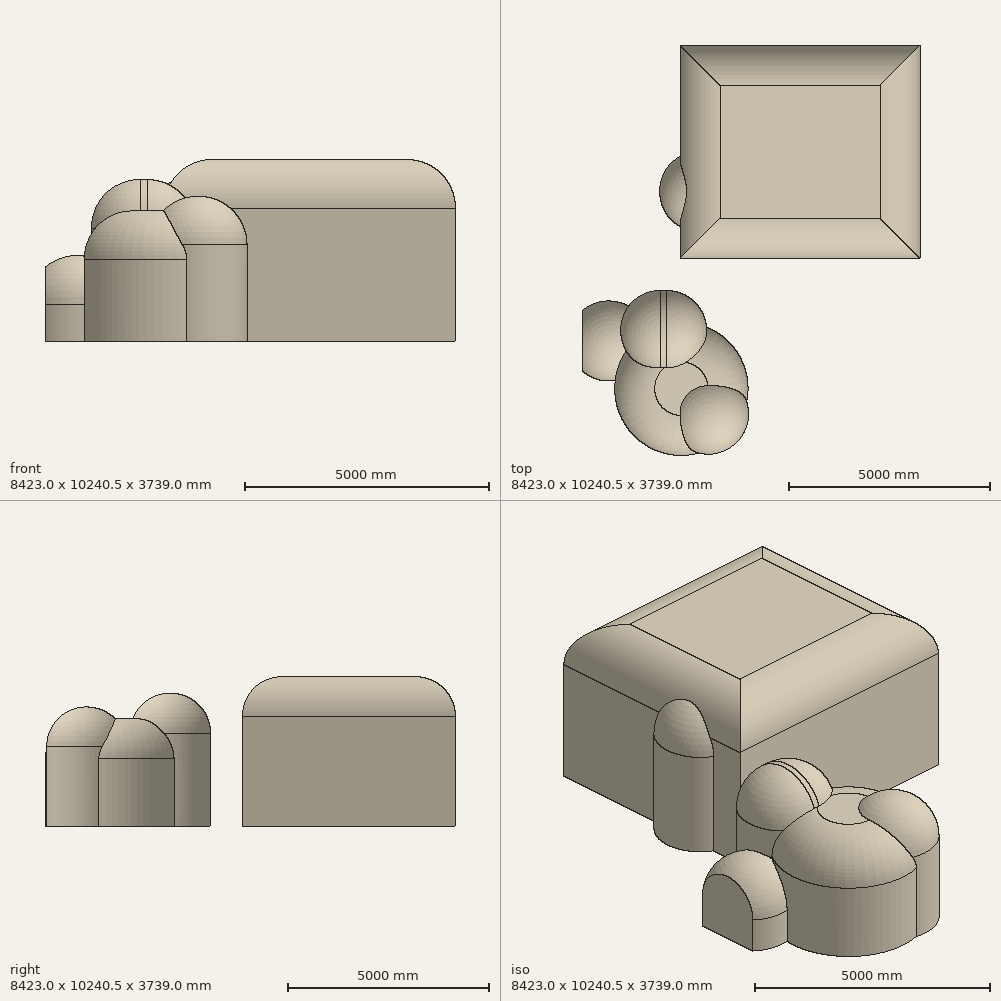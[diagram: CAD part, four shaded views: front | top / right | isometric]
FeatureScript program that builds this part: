
annotation { "Feature Type Name" : "Feature", "Feature Type Description" : "" }
export const myFeature = defineFeature(function(context is Context, id is Id, definition is map)
    precondition{}
    {
        {
            var Q0;
            Q0=qCreatedBy(makeId("Top.planeOp"),FACE);
            var sketch = newSketch(context, id + "F0", { "sketchPlane" : qUnion([Q0])});
            skLineSegment(sketch, "E0", {"start": v(0, 0) * mm, "end": v(7972, 0) * mm});
            skLineSegment(sketch, "E1", {"start": v(0, 0) * mm, "end": v(0, 5130) * mm});
            skLineSegment(sketch, "E2", {"start": v(0, 5130) * mm, "end": v(355, 5130) * mm});
            skLineSegment(sketch, "E3", {"start": v(355, 5130) * mm, "end": v(355, 15952) * mm});
            skLineSegment(sketch, "E4.bottom", {"start": v(2435, 10830) * mm, "end": v(8423, 10830) * mm});
            skLineSegment(sketch, "E4.top", {"start": v(2435, 5511) * mm, "end": v(8423, 5511) * mm});
            skLineSegment(sketch, "E4.left", {"start": v(2435, 10830) * mm, "end": v(2435, 5511) * mm});
            skLineSegment(sketch, "E4.right", {"start": v(8423, 10830) * mm, "end": v(8423, 5511) * mm});
            skCircle(sketch, "E5", {"center": v(2917, 7181) * mm, "radius": 1000 * mm});
            skCircle(sketch, "E6", {"center": v(650, 3450) * mm, "radius": 1000 * mm});
            skArc(sketch, "E7", {"start": v(1944, 4712) * mm, "mid": v(944, 3712) * mm, "end": v(1944, 2712) * mm});
            skArc(sketch, "E8", {"start": v(2091, 2712) * mm, "mid": v(3091, 3712) * mm, "end": v(2091, 4712) * mm});
            skLineSegment(sketch, "E9", {"start": v(1944, 4712) * mm, "end": v(2091, 4712) * mm});
            skLineSegment(sketch, "E10", {"start": v(1944, 2712) * mm, "end": v(2091, 2712) * mm});
            skCircle(sketch, "E11", {"center": v(3141, 1620) * mm, "radius": 1000 * mm});
            skSolve(sketch);
        }
        {
            var Q0;
            {var subQ0=sQuery(id+"F0.wireOp",EDGE,"E5");var subQ1=sQuery(id+"F0.wireOp",EDGE,"E4.left");var subQ2=makeQuery(id+"F0.imprint","INTERSECT",VERTEX,{"disambiguationData":[OD(0.0)],"derivedFrom":[subQ1,subQ0]});Q0=makeQuery(id+"F0.imprint","IMPRINT",FACE,{"disambiguationData":[TD([[makeQuery(id+"F0.imprint","IMPRINT",EDGE,{"disambiguationData":[TD([[subQ2,-1.0]])],"derivedFrom":subQ1}),-1.0]])]});}
            var Q1;
            {var subQ0=sQuery(id+"F0.wireOp",EDGE,"E5");var subQ1=sQuery(id+"F0.wireOp",EDGE,"E4.left");var subQ2=makeQuery(id+"F0.imprint","INTERSECT",VERTEX,{"disambiguationData":[OD(0.0)],"derivedFrom":[subQ1,subQ0]});Q1=makeQuery(id+"F0.imprint","IMPRINT",FACE,{"disambiguationData":[TD([[makeQuery(id+"F0.imprint","IMPRINT",EDGE,{"disambiguationData":[TD([[subQ2,-1.0]])],"derivedFrom":subQ1}),1.0]])]});}
            extrude(context, id + "F1", {"entities" : qUnion([Q0, Q1]), "depth" : 3327 * mm});
        }
        {
            var Q0;
            Q0=makeQuery(id+"F1.opExtrude","CAP_EDGE",EDGE,{"disambiguationData":[OSD([sQuery(id+"F0.wireOp",EDGE,"E5")])],"isStart":false});
            fillet(context, id + "F2", {"entities" : qUnion([Q0]), "radius" : 1000 * mm, "tangentPropagation" : true, "allowEdgeOverflow" : false});
        }
        {
            var Q0;
            {var subQ4=sQuery(id+"F0.wireOp",EDGE,"E4.bottom");Q0=makeQuery(id+"F0.imprint","IMPRINT",FACE,{"disambiguationData":[TD([[makeQuery(id+"F0.imprint","IMPRINT",EDGE,{"derivedFrom":subQ4}),-1.0]])]});}
            var Q1;
            {var subQ0=sQuery(id+"F0.wireOp",EDGE,"E5");var subQ1=sQuery(id+"F0.wireOp",EDGE,"E4.left");var subQ2=makeQuery(id+"F0.imprint","INTERSECT",VERTEX,{"disambiguationData":[OD(0.0)],"derivedFrom":[subQ1,subQ0]});Q1=makeQuery(id+"F0.imprint","IMPRINT",FACE,{"disambiguationData":[TD([[makeQuery(id+"F0.imprint","IMPRINT",EDGE,{"disambiguationData":[TD([[subQ2,-1.0]])],"derivedFrom":subQ1}),1.0]])]});}
            extrude(context, id + "F3", {"entities" : qUnion([Q0, Q1]), "operationType" : NewBodyOperationType.ADD, "depth" : 3739 * mm});
        }
        {
            var Q0;
            Q0=makeQuery(id+"F3.opExtrude","CAP_EDGE",EDGE,{"disambiguationData":[OSD([sQuery(id+"F0.wireOp",EDGE,"E4.top")])],"isStart":false});
            var Q1;
            Q1=makeQuery(id+"F3.opExtrude","CAP_EDGE",EDGE,{"disambiguationData":[OSD([sQuery(id+"F0.wireOp",EDGE,"E4.right")])],"isStart":false});
            var Q2;
            Q2=makeQuery(id+"F3.opExtrude","CAP_EDGE",EDGE,{"disambiguationData":[OSD([sQuery(id+"F0.wireOp",EDGE,"E4.left")])],"isStart":false});
            var Q3;
            Q3=makeQuery(id+"F3.opExtrude","CAP_EDGE",EDGE,{"disambiguationData":[OSD([sQuery(id+"F0.wireOp",EDGE,"E4.bottom")])],"isStart":false});
            fillet(context, id + "F4", {"entities" : qUnion([Q0, Q1, Q2, Q3]), "radius" : 1000 * mm, "tangentPropagation" : true, "allowEdgeOverflow" : false});
        }
        {
            var Q0;
            {var subQ0=sQuery(id+"F0.wireOp",EDGE,"E6");var subQ1=sQuery(id+"F0.wireOp",EDGE,"E1");var subQ2=makeQuery(id+"F0.imprint","INTERSECT",VERTEX,{"disambiguationData":[OD(0.0)],"derivedFrom":[subQ1,subQ0]});Q0=makeQuery(id+"F0.imprint","IMPRINT",FACE,{"disambiguationData":[TD([[makeQuery(id+"F0.imprint","IMPRINT",EDGE,{"disambiguationData":[TD([[subQ2,1.0]])],"derivedFrom":subQ1}),-1.0]])]});}
            var Q1;
            {var subQ0=sQuery(id+"F0.wireOp",EDGE,"E7");var subQ1=sQuery(id+"F0.wireOp",EDGE,"E6");var subQ2=makeQuery(id+"F0.imprint","INTERSECT",VERTEX,{"disambiguationData":[OD(0.0)],"derivedFrom":[subQ1,subQ0]});Q1=makeQuery(id+"F0.imprint","IMPRINT",FACE,{"disambiguationData":[TD([[makeQuery(id+"F0.imprint","IMPRINT",EDGE,{"disambiguationData":[TD([[subQ2,1.0]])],"derivedFrom":subQ1}),1.0]])]});}
            extrude(context, id + "F5", {"entities" : qUnion([Q0, Q1]), "depth" : 1765 * mm});
        }
        {
            var Q0;
            Q0=makeQuery(id+"F5.opExtrude","CAP_EDGE",EDGE,{"disambiguationData":[OSD([sQuery(id+"F0.wireOp",EDGE,"E6")])],"isStart":false});
            fillet(context, id + "F6", {"entities" : qUnion([Q0]), "radius" : 1000 * mm, "tangentPropagation" : true, "allowEdgeOverflow" : false});
        }
        {
            var Q0;
            Q0=makeQuery(id+"F0.imprint","IMPRINT",FACE,{"disambiguationData":[TD([[makeQuery(id+"F0.imprint","IMPRINT",EDGE,{"derivedFrom":sQuery(id+"F0.wireOp",EDGE,"E8")}),1.0]])]});
            var Q1;
            {var subQ0=sQuery(id+"F0.wireOp",EDGE,"E7");var subQ1=sQuery(id+"F0.wireOp",EDGE,"E6");var subQ2=makeQuery(id+"F0.imprint","INTERSECT",VERTEX,{"disambiguationData":[OD(0.0)],"derivedFrom":[subQ1,subQ0]});Q1=makeQuery(id+"F0.imprint","IMPRINT",FACE,{"disambiguationData":[TD([[makeQuery(id+"F0.imprint","IMPRINT",EDGE,{"disambiguationData":[TD([[subQ2,1.0]])],"derivedFrom":subQ1}),1.0]])]});}
            extrude(context, id + "F7", {"entities" : qUnion([Q0, Q1]), "operationType" : NewBodyOperationType.ADD, "depth" : 3327 * mm});
        }
        {
            var Q0;
            Q0=makeQuery(id+"F7.opExtrude","CAP_EDGE",EDGE,{"disambiguationData":[OSD([sQuery(id+"F0.wireOp",EDGE,"E7")])],"isStart":false});
            fillet(context, id + "F8", {"entities" : qUnion([Q0]), "radius" : 1000 * mm, "tangentPropagation" : true, "allowEdgeOverflow" : false});
        }
        {
            var Q0;
            Q0=makeQuery(id+"F0.imprint","IMPRINT",FACE,{"disambiguationData":[TD([[makeQuery(id+"F0.imprint","IMPRINT",EDGE,{"derivedFrom":sQuery(id+"F0.wireOp",EDGE,"E11")}),1.0]])]});
            extrude(context, id + "F9", {"entities" : qUnion([Q0]), "depth" : 2984 * mm});
        }
        {
            var Q0;
            Q0=makeQuery(id+"F9.opExtrude","CAP_EDGE",EDGE,{"disambiguationData":[OSD([sQuery(id+"F0.wireOp",EDGE,"E11")])],"isStart":false});
            fillet(context, id + "F10", {"entities" : qUnion([Q0]), "radius" : 1000 * mm, "tangentPropagation" : true, "allowEdgeOverflow" : false});
        }
        {
            var Q0;
            Q0=qCreatedBy(makeId("Top.planeOp"),FACE);
            var sketch = newSketch(context, id + "F11", { "sketchPlane" : qUnion([Q0])});
            skCircle(sketch, "E12.0", {"center": v(650, 3450) * mm, "radius": 1000 * mm});
            skLineSegment(sketch, "E13.0", {"start": v(0, 0) * mm, "end": v(7972, 0) * mm});
            skLineSegment(sketch, "E14.0", {"start": v(0, 0) * mm, "end": v(0, 5130) * mm});
            skLineSegment(sketch, "E15.0", {"start": v(355, 5130) * mm, "end": v(355, 15952) * mm, "construction": true});
            skCircle(sketch, "E16", {"center": v(2461, 2256) * mm, "radius": 1666.5 * mm});
            skCircle(sketch, "E17", {"center": v(5761, 6751) * mm, "radius": 1000 * mm});
            skArc(sketch, "E18", {"start": v(4969.67, 9882.39) * mm, "mid": v(5149.61, 8479.67) * mm, "end": v(6552.33, 8659.61) * mm});
            skArc(sketch, "E19", {"start": v(6834.33, 9024.61) * mm, "mid": v(6654.39, 10427.33) * mm, "end": v(5251.67, 10247.39) * mm});
            skLineSegment(sketch, "E20", {"start": v(6552.33, 8659.61) * mm, "end": v(6834.33, 9024.61) * mm});
            skLineSegment(sketch, "E21", {"start": v(4969.67, 9882.39) * mm, "end": v(5251.67, 10247.39) * mm});
            skSolve(sketch);
        }
        {
            var Q0;
            {var subQ0=sQuery(id+"F11.wireOp",EDGE,"E14.0");var subQ1=sQuery(id+"F11.wireOp",EDGE,"E12.0");var subQ2=makeQuery(id+"F11.imprint","INTERSECT",VERTEX,{"disambiguationData":[OD(0.0)],"derivedFrom":[subQ1,subQ0]});Q0=makeQuery(id+"F11.imprint","IMPRINT",FACE,{"disambiguationData":[TD([[makeQuery(id+"F11.imprint","IMPRINT",EDGE,{"disambiguationData":[TD([[subQ2,1.0]])],"derivedFrom":subQ1}),1.0]])]});}
            var Q1;
            {var subQ0=sQuery(id+"F11.wireOp",EDGE,"E16");var subQ1=sQuery(id+"F11.wireOp",EDGE,"E12.0");var subQ2=makeQuery(id+"F11.imprint","INTERSECT",VERTEX,{"disambiguationData":[OD(0.0)],"derivedFrom":[subQ1,subQ0]});Q1=makeQuery(id+"F11.imprint","IMPRINT",FACE,{"disambiguationData":[TD([[makeQuery(id+"F11.imprint","IMPRINT",EDGE,{"disambiguationData":[TD([[subQ2,1.0]])],"derivedFrom":subQ1}),1.0]])]});}
            extrude(context, id + "F12", {"entities" : qUnion([Q0, Q1]), "depth" : 1400 * mm});
        }
        {
            var Q0;
            Q0=makeQuery(id+"F12.opExtrude","CAP_EDGE",EDGE,{"disambiguationData":[OSD([sQuery(id+"F11.wireOp",EDGE,"E12.0")])],"isStart":false});
            fillet(context, id + "F13", {"entities" : qUnion([Q0]), "radius" : 1000 * mm, "tangentPropagation" : true, "allowEdgeOverflow" : false});
        }
        {
            var Q0;
            {var subQ0=sQuery(id+"F11.wireOp",EDGE,"E16");var subQ1=sQuery(id+"F11.wireOp",EDGE,"E12.0");var subQ2=makeQuery(id+"F11.imprint","INTERSECT",VERTEX,{"disambiguationData":[OD(0.0)],"derivedFrom":[subQ1,subQ0]});Q0=makeQuery(id+"F11.imprint","IMPRINT",FACE,{"disambiguationData":[TD([[makeQuery(id+"F11.imprint","IMPRINT",EDGE,{"disambiguationData":[TD([[subQ2,1.0]])],"derivedFrom":subQ1}),-1.0]])]});}
            var Q1;
            {var subQ0=sQuery(id+"F11.wireOp",EDGE,"E16");var subQ1=sQuery(id+"F11.wireOp",EDGE,"E12.0");var subQ2=makeQuery(id+"F11.imprint","INTERSECT",VERTEX,{"disambiguationData":[OD(0.0)],"derivedFrom":[subQ1,subQ0]});Q1=makeQuery(id+"F11.imprint","IMPRINT",FACE,{"disambiguationData":[TD([[makeQuery(id+"F11.imprint","IMPRINT",EDGE,{"disambiguationData":[TD([[subQ2,1.0]])],"derivedFrom":subQ1}),1.0]])]});}
            extrude(context, id + "F14", {"entities" : qUnion([Q0, Q1]), "operationType" : NewBodyOperationType.ADD, "depth" : 2683 * mm});
        }
        {
            var Q0;
            Q0=makeQuery(id+"F14.opExtrude","CAP_EDGE",EDGE,{"disambiguationData":[OSD([sQuery(id+"F11.wireOp",EDGE,"E16")])],"isStart":false});
            fillet(context, id + "F15", {"entities" : qUnion([Q0]), "radius" : 1000 * mm, "tangentPropagation" : true, "allowEdgeOverflow" : false});
        }
        {
            var Q0;
            {var subQ0=sQuery(id+"F11.wireOp",EDGE,"E19");var subQ1=sQuery(id+"F11.wireOp",EDGE,"E18");var subQ2=makeQuery(id+"F11.imprint","INTERSECT",VERTEX,{"disambiguationData":[OD(0.0)],"derivedFrom":[subQ1,subQ0]});Q0=makeQuery(id+"F11.imprint","IMPRINT",FACE,{"disambiguationData":[TD([[makeQuery(id+"F11.imprint","IMPRINT",EDGE,{"disambiguationData":[TD([[subQ2,1.0]])],"derivedFrom":subQ1}),-1.0]])]});}
            var Q1;
            {var subQ0=sQuery(id+"F11.wireOp",EDGE,"E19");var subQ1=sQuery(id+"F11.wireOp",EDGE,"E18");var subQ2=makeQuery(id+"F11.imprint","INTERSECT",VERTEX,{"disambiguationData":[OD(0.0)],"derivedFrom":[subQ1,subQ0]});Q1=makeQuery(id+"F11.imprint","IMPRINT",FACE,{"disambiguationData":[TD([[makeQuery(id+"F11.imprint","IMPRINT",EDGE,{"disambiguationData":[TD([[subQ2,1.0]])],"derivedFrom":subQ1}),1.0]])]});}
            var Q2;
            Q2=makeQuery(id+"F11.imprint","IMPRINT",FACE,{"disambiguationData":[TD([[makeQuery(id+"F11.imprint","IMPRINT",EDGE,{"derivedFrom":sQuery(id+"F11.wireOp",EDGE,"E17")}),1.0]])]});
            extrude(context, id + "F16", {"entities" : qUnion([Q0, Q1, Q2]), "depth" : 2550 * mm});
        }
        {
            var Q0;
            Q0=makeQuery(id+"F16.opExtrude","CAP_EDGE",EDGE,{"disambiguationData":[OSD([sQuery(id+"F11.wireOp",EDGE,"E19")])],"isStart":false});
            var Q1;
            Q1=makeQuery(id+"F16.opExtrude","CAP_EDGE",EDGE,{"disambiguationData":[OSD([sQuery(id+"F11.wireOp",EDGE,"E17")])],"isStart":false});
            fillet(context, id + "F17", {"entities" : qUnion([Q0, Q1]), "radius" : 1000 * mm, "tangentPropagation" : true, "allowEdgeOverflow" : false});
        }
    });
